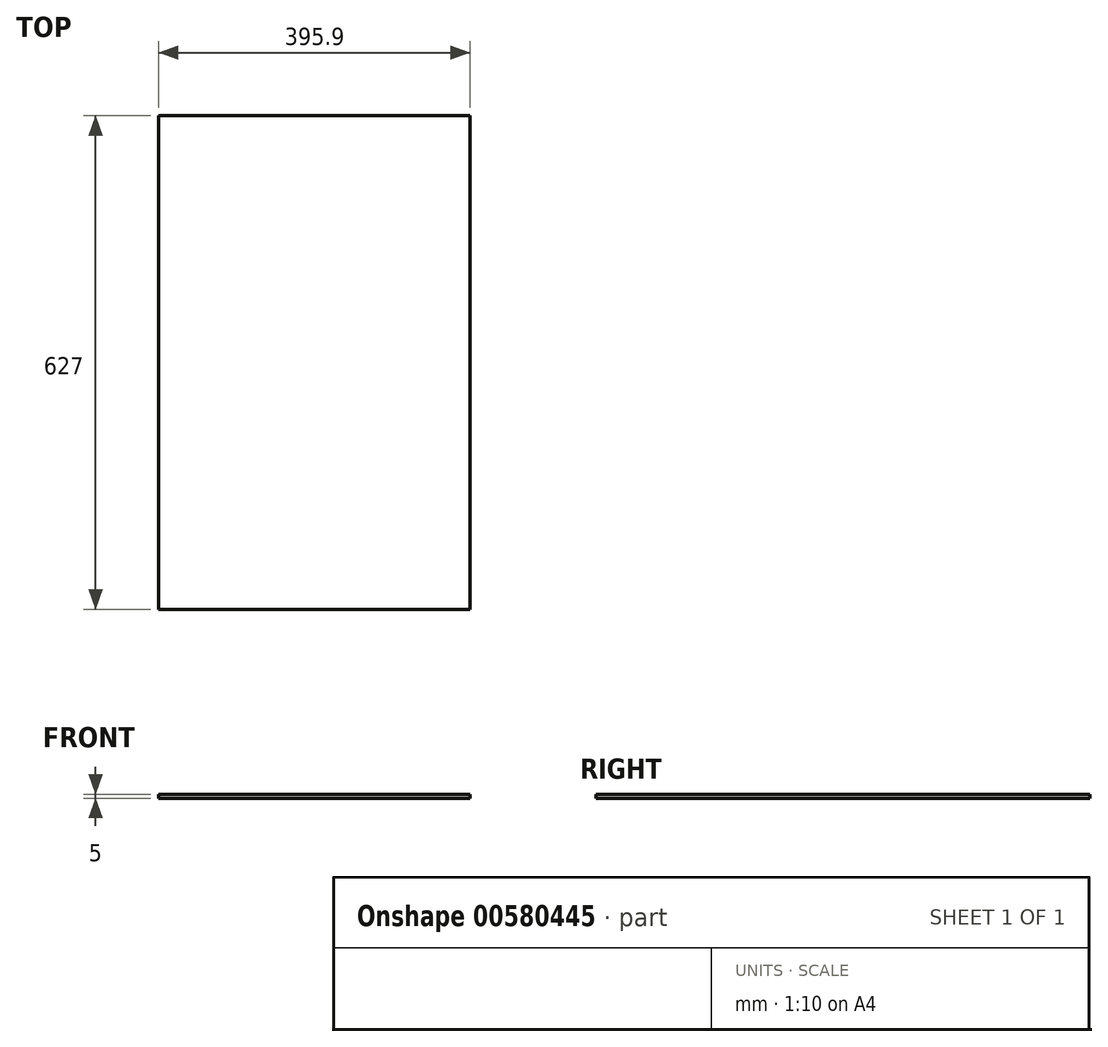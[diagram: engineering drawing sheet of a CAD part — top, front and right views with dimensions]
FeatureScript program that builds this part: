
annotation { "Feature Type Name" : "Feature", "Feature Type Description" : "" }
export const myFeature = defineFeature(function(context is Context, id is Id, definition is map)
    precondition{}
    {
        {
            var Q0;
            Q0=qCreatedBy(makeId("Top.planeOp"),FACE);
            var sketch = newSketch(context, id + "F0", { "sketchPlane" : qUnion([Q0])});
            skLineSegment(sketch, "E0.bottom", {"start": v(-250.12, 560.53) * mm, "end": v(145.78, 560.53) * mm});
            skLineSegment(sketch, "E0.top", {"start": v(-250.12, -66.47) * mm, "end": v(145.78, -66.47) * mm});
            skLineSegment(sketch, "E0.left", {"start": v(-250.12, 560.53) * mm, "end": v(-250.12, -66.47) * mm});
            skLineSegment(sketch, "E0.right", {"start": v(145.78, 560.53) * mm, "end": v(145.78, -66.47) * mm});
            skSolve(sketch);
        }
        {
            var Q0;
            Q0=makeQuery(id+"F0.imprint","IMPRINT",FACE,{"disambiguationData":[TD([[makeQuery(id+"F0.imprint","IMPRINT",EDGE,{"derivedFrom":sQuery(id+"F0.wireOp",EDGE,"E0.bottom")}),-1.0]])]});
            extrude(context, id + "F1", {"entities" : qUnion([Q0]), "depth" : 5 * mm, "offsetDistance" : 25 * mm});
        }
    });
